# Revit family: Hager-Univers-IP44-D161-Cl.II-FWB-encl--NoHosted-AT-de
name_source: partatom
category: Equipement électrique
units: mm (PartAtom-declared; Revit-internal decimal feet)

## family parameters
Basée sur le plan de construction = Oui
Configuration du panneau = Deux colonnes, circuits au sein
Cote de connecteur circulaire = Utiliser le diamètre
Couper avec des vides une fois chargée = Non
Partagée = Non
Point de calcul de pièce = Non
Toujours verticalement = Oui
Type d'élément = Tableau de raccordement

## types (21) — shared parameters
Commentaires du type = Univers
EF000003 - Montageart = EV000384 - Aufputz
EF000007 - Farbe = EV000202 - weiß
EF000049 - Tiefe = 161 mm  [stored 0.528215 ft]
EF000116 - RAL-Nummer = 9010
EF001088 - Anbaumöglichkeit = Oui
EF001596 - Werkstoff des Gehäuses = EV000179 - Stahl
EF001613 - Funktionserhalt = EV000494 - ohne
EF002950 - Breite in Teilungseinheiten = 12
EF003532 - Geeignet für Außengebrauch = Non
EF004293 - Schlagfestigkeit = EV006815 - IK09
EF005474 - Schutzart (IP) = EV006418 - IP44
EF006244 - Transparenter Deckel/Tür = Non
EF006306 - Mit Schloss = Non
EF007800 - Geeignet für Blitzschutz = Non
EF008873 - Nennstrom (In) = 125 A
EF015940 - Deckel mit Überdruckentlastung = Non
Elévation par défaut = 1219 mm
Fabricant = Hager
HG000002 - Mit tür = Oui
HG000003 - Bereich = Univers
HG000006 - Unterputz = Non
HG000023 - Gehäuse mit doppeltem Querschnitt = Non
HG000024 - Höhe des unteren Teils = 600 mm
HG000026 - Stehend auf dem Boden = Non
zero-valued in all types: EF000218 - Einbautiefe, HG000027 - Sockelhöhe

## per-type parameters (varying)
| type | EF000008 - Breite | EF000040 - Höhe | EF000118 - Mit Montageplatte | EF000266 - Anzahl der Reihen | EF000339 - Art der Abdeckung | EF000437 - Anzahl der Leitungseinführungen | EF001131 - Innentiefe | EF004427 - Anzahl der Module | EF004464 - Art der Tür | EF009170 - Materialstärke Gehäuse | EF009171 - Materialstärke Tür/Deckel | EF009212 - Ausführung Deckel | EF009554 - Anzahl der Öffnungen für Flanschplatten | HG000004 - Herstellerreferenz | HG000009 - Doppelflügeligen Tür | HG000010 - Asymmetrische Türen |
| Aufputz IP44 B1050 H1100 T161  - FWB74D | 1050 mm | 1100 mm | Non | 0 | EV000494 - ohne | 16 | 160 mm  [stored 0.524934 ft] | 336 | EV000494 - ohne | 1 mm  [stored 0.00328084 ft] | 1 mm  [stored 0.00328084 ft] | EV000116 - geschlossen | 8 | FWB74D | Oui | Non |
| Aufputz IP44 B1050 H500 T161  - FWB34D | 1050 mm | 500 mm  [stored 1.64042 ft] | Non | 0 | EV004216 - Tür | 16 | 156 mm  [stored 0.511811 ft] | 144 | EV003602 - Doppel | 1 mm  [stored 0.00328084 ft] | 1 mm  [stored 0.00328084 ft] | EV000116 - geschlossen | 8 | FWB34D | Oui | Non |
| Aufputz IP44 B1050 H650 T161  - FWB44D | 1050 mm | 650 mm  [stored 2.13255 ft] | Non | 0 | EV004216 - Tür | 16 | 156 mm  [stored 0.511811 ft] | 192 | EV003602 - Doppel | 1 mm  [stored 0.00328084 ft] | 1 mm  [stored 0.00328084 ft] | EV000116 - geschlossen | 8 | FWB44D | Oui | Non |
| Aufputz IP44 B1050 H800 T161  - FWB54D | 1050 mm | 800 mm  [stored 2.62467 ft] | Non | 0 | EV004216 - Tür | 16 | 156 mm  [stored 0.511811 ft] | 240 | EV002646 - Einzel | 1 mm  [stored 0.00328084 ft] | 1 mm  [stored 0.00328084 ft] | EV000116 - geschlossen | 8 | FWB54D | Oui | Non |
| Aufputz IP44 B1050 H950 T161  - FWB64D | 1050 mm | 950 mm  [stored 3.1168 ft] | Non | 0 | EV004216 - Tür | 16 | 156 mm  [stored 0.511811 ft] | 288 | EV003602 - Doppel | 1 mm  [stored 0.00328084 ft] | 1 mm  [stored 0.00328084 ft] | EV000116 - geschlossen | 8 | FWB64D | Oui | Non |
| Aufputz IP44 B300 H1100 T161  - FWB71D | 300 mm | 1100 mm | Non | 0 | EV004216 - Tür | 4 | 160 mm  [stored 0.524934 ft] | 84 | EV000494 - ohne | 1 mm  [stored 0.00328084 ft] | 1 mm  [stored 0.00328084 ft] | EV000116 - geschlossen | 2 | FWB71D | Non | Non |
| Aufputz IP44 B300 H1250 T161  - FWB81D | 300 mm | 1250 mm  [stored 4.10105 ft] | Non | 8 | EV004216 - Tür | 4 | 161 mm  [stored 0.528215 ft] | 12 | EV000494 - ohne | 1 mm  [stored 0.00328084 ft] | 1 mm  [stored 0.00328084 ft] | EV000116 - geschlossen | 2 | FWB81D | Non | Non |
| Aufputz IP44 B300 H500 T161  - FWQ31P | 300 mm | 500 mm  [stored 1.64042 ft] | Oui | 1 | EV001012 - Deckel | 4 | 161 mm  [stored 0.528215 ft] | 36 | EV002646 - Einzel | 2 mm  [stored 0.00656168 ft] | 2 mm  [stored 0.00656168 ft] | EV009916 - mit Ausschnitt | 2 | FWQ31P | Non | Non |
| Aufputz IP44 B300 H650 T161  - FWB41D | 300 mm | 650 mm  [stored 2.13255 ft] | Non | 0 | EV004216 - Tür | 4 | 160 mm  [stored 0.524934 ft] | 48 | EV000494 - ohne | 2 mm  [stored 0.00656168 ft] | 2 mm  [stored 0.00656168 ft] | EV000116 - geschlossen | 2 | FWB41D | Non | Non |
| Aufputz IP44 B300 H800 T161  - FWB51D | 300 mm | 800 mm  [stored 2.62467 ft] | Non | 0 | EV004216 - Tür | 4 | 160 mm  [stored 0.524934 ft] | 60 | EV000494 - ohne | 1 mm  [stored 0.00328084 ft] | 1 mm  [stored 0.00328084 ft] | EV000116 - geschlossen | 2 | FWB51D | Non | Non |
| Aufputz IP44 B300 H950 T161  - FWB61D | 300 mm | 950 mm  [stored 3.1168 ft] | Non | 0 | EV004216 - Tür | 4 | 160 mm  [stored 0.524934 ft] | 72 | EV000494 - ohne | 1 mm  [stored 0.00328084 ft] | 1 mm  [stored 0.00328084 ft] | EV000116 - geschlossen | 2 | FWB61D | Non | Non |
| Aufputz IP44 B550 H1100 T161  - FWB72D | 550 mm | 1100 mm | Non | 0 | EV004216 - Tür | 8 | 160 mm  [stored 0.524934 ft] | 168 | EV000494 - ohne | 1 mm  [stored 0.00328084 ft] | 1 mm  [stored 0.00328084 ft] | EV000116 - geschlossen | 4 | FWB72D | Non | Non |
| Aufputz IP44 B550 H500 T161  - FWB32D | 550 mm | 500 mm  [stored 1.64042 ft] | Non | 0 | EV000494 - ohne | 8 | 156 mm  [stored 0.511811 ft] | 72 | EV002646 - Einzel | 2 mm  [stored 0.00656168 ft] | 2 mm  [stored 0.00656168 ft] | EV000116 - geschlossen | 4 | FWB32D | Non | Non |
| Aufputz IP44 B550 H650 T161  - FWB42D | 550 mm | 650 mm  [stored 2.13255 ft] | Non | 0 | EV004216 - Tür | 8 | 160 mm  [stored 0.524934 ft] | 96 | EV000494 - ohne | 1 mm  [stored 0.00328084 ft] | 1 mm  [stored 0.00328084 ft] | EV000116 - geschlossen | 4 | FWB42D | Non | Non |
| Aufputz IP44 B550 H800 T161  - FWB52D | 550 mm | 800 mm  [stored 2.62467 ft] | Non | 0 | EV004216 - Tür | 8 | 160 mm  [stored 0.524934 ft] | 120 | EV000494 - ohne | 1 mm  [stored 0.00328084 ft] | 1 mm  [stored 0.00328084 ft] | EV000116 - geschlossen | 4 | FWB52D | Non | Non |
| Aufputz IP44 B550 H950 T161  - FWB62D | 550 mm | 950 mm  [stored 3.1168 ft] | Non | 0 | EV004216 - Tür | 8 | 160 mm  [stored 0.524934 ft] | 144 | EV000494 - ohne | 1 mm  [stored 0.00328084 ft] | 1 mm  [stored 0.00328084 ft] | EV000116 - geschlossen | 4 | FWB62D | Non | Non |
| Aufputz IP44 B800 H1100 T161  - FWB73D | 800 mm  [stored 2.62467 ft] | 1100 mm | Non | 0 | EV004216 - Tür | 12 | 156 mm  [stored 0.511811 ft] | 252 | EV003602 - Doppel | 1 mm  [stored 0.00328084 ft] | 1 mm  [stored 0.00328084 ft] | EV000116 - geschlossen | 6 | FWB73D | Oui | Oui |
| Aufputz IP44 B800 H500 T161  - FWB33D | 800 mm  [stored 2.62467 ft] | 500 mm  [stored 1.64042 ft] | Non | 0 | EV004216 - Tür | 12 | 160 mm  [stored 0.524934 ft] | 108 | EV000494 - ohne | 1 mm  [stored 0.00328084 ft] | 1 mm  [stored 0.00328084 ft] | EV000116 - geschlossen | 6 | FWB33D | Oui | Oui |
| Aufputz IP44 B800 H650 T161  - FWB43D | 800 mm  [stored 2.62467 ft] | 650 mm  [stored 2.13255 ft] | Non | 0 | EV004216 - Tür | 12 | 160 mm  [stored 0.524934 ft] | 144 | EV000494 - ohne | 2 mm  [stored 0.00656168 ft] | 1 mm  [stored 0.00328084 ft] | EV009916 - mit Ausschnitt | 6 | FWB43D | Oui | Oui |
| Aufputz IP44 B800 H800 T161  - FWB53D | 800 mm  [stored 2.62467 ft] | 800 mm  [stored 2.62467 ft] | Non | 0 | EV004216 - Tür | 12 | 160 mm  [stored 0.524934 ft] | 180 | EV000494 - ohne | 2 mm  [stored 0.00656168 ft] | 1 mm  [stored 0.00328084 ft] | EV000116 - geschlossen | 6 | FWB53D | Oui | Oui |
| Aufputz IP44 B800 H950 T161  - FWB63D | 800 mm  [stored 2.62467 ft] | 950 mm  [stored 3.1168 ft] | Non | 0 | EV004216 - Tür | 12 | 156 mm  [stored 0.511811 ft] | 216 | EV000494 - ohne | 1 mm  [stored 0.00328084 ft] | 1 mm  [stored 0.00328084 ft] | EV000116 - geschlossen | 6 | FWB63D | Oui | Oui |

note: [stored X ft] marks values corroborated as IEEE doubles in the binary element streams (Revit-internal decimal feet)

## geometry (parser evidence)
native form markers: Blend x4, Sweep x9
no freeform markers — native parametric forms only
